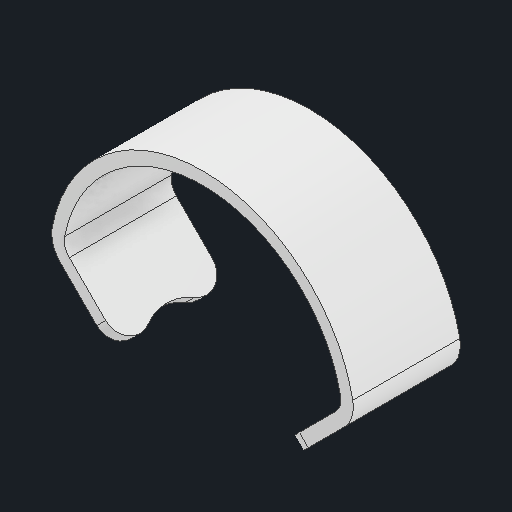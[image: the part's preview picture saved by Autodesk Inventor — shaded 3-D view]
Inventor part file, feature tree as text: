
AUTODESK INVENTOR PART (.ipt)
format: ipt  version: 2023 (Build 270158000, 158)  size: 113,152 bytes
history: native  units: in
note: dims shown in document units (in); Inventor stores cm internally (conversion verified against a paired STEP export)
features: mirror x1
ambient origin geometry x8: Origin, YZ Plane, XZ Plane, XY Plane, X Axis, Y Axis, Z Axis, Center Point
bodies: Solid1 (feature_tree)
feature tree (1):
  mirror  "Mirror1"
